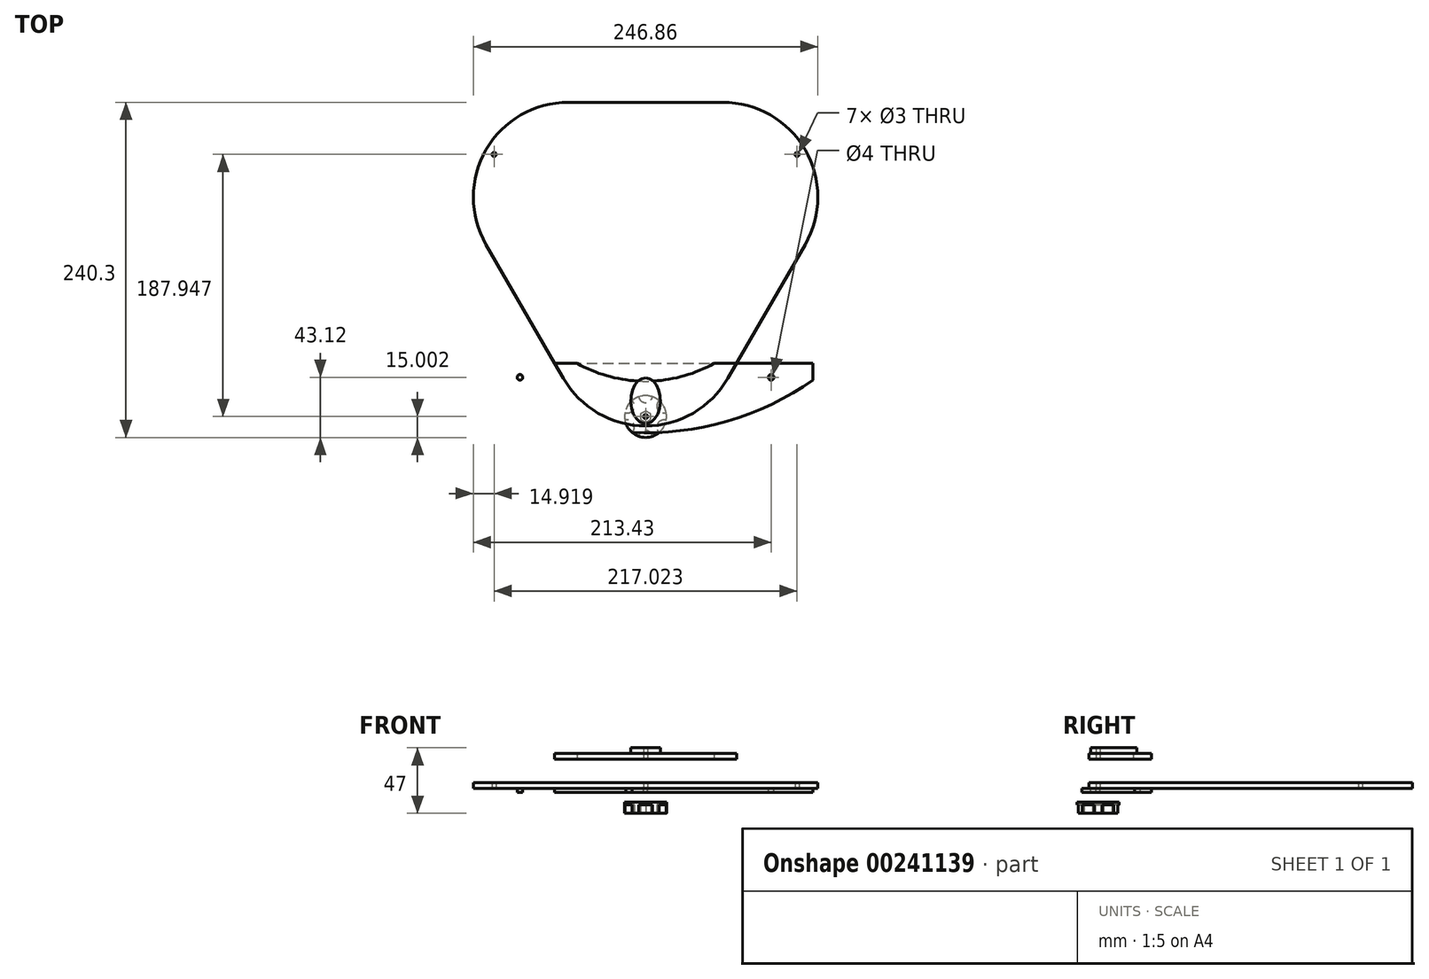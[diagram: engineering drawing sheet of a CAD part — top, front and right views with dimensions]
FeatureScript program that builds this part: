
annotation { "Feature Type Name" : "Feature", "Feature Type Description" : "" }
export const myFeature = defineFeature(function(context is Context, id is Id, definition is map)
    precondition{}
    {
        {
            var Q0;
            Q0=qCreatedBy(makeId("Top.planeOp"),FACE);
            var sketch = newSketch(context, id + "F0", { "sketchPlane" : qUnion([Q0])});
            skLineSegment(sketch, "E0.bottom", {"start": v(-120, -87.18) * mm, "end": v(120, -87.18) * mm});
            skLineSegment(sketch, "E0.top", {"start": v(-120, -107.18) * mm, "end": v(120, -107.18) * mm, "construction": true});
            skCircle(sketch, "E1", {"center": v(0, 0) * mm, "radius": 100 * mm, "construction": true});
            skCircle(sketch, "E2.1.0", {"center": v(-90, -97.18) * mm, "radius": 2 * mm});
            skCircle(sketch, "E2.1.2", {"center": v(90, -97.18) * mm, "radius": 2 * mm});
            skArc(sketch, "E3", {"start": v(-134.08, -88.82) * mm, "mid": v(-0.24, -137) * mm, "end": v(133.6, -88.82) * mm});
            skLineSegment(sketch, "E4", {"start": v(-120, -87.18) * mm, "end": v(-120, -99.5) * mm});
            skCircle(sketch, "E5", {"center": v(0, -125.3) * mm, "radius": 15 * mm});
            skPoint(sketch, "E5.centerSnap0", {"position": v(0, -107.18) * mm});
            skCircle(sketch, "E6", {"center": v(0, -125.3) * mm, "radius": 1.5 * mm});
            skLineSegment(sketch, "E7", {"start": v(120, -87.18) * mm, "end": v(120, -99.17) * mm});
            skCircle(sketch, "E8.cCircle", {"center": v(0, 0) * mm, "radius": 100 * mm});
            skLineSegment(sketch, "E8.0", {"start": v(-55.43, 100) * mm, "end": v(55.43, 100) * mm});
            skLineSegment(sketch, "E8.1", {"start": v(114.32, -2) * mm, "end": v(58.89, -98) * mm});
            skLineSegment(sketch, "E8.2", {"start": v(-58.89, -98) * mm, "end": v(-114.32, -2) * mm});
            skPoint(sketch, "E8.0.midPoint", {"position": v(0, 100) * mm});
            skCircle(sketch, "E9.1.0", {"center": v(108.51, 62.65) * mm, "radius": 1.5 * mm});
            skCircle(sketch, "E9.2.0", {"center": v(-108.51, 62.65) * mm, "radius": 1.5 * mm});
            skPoint(sketch, "E10.visualSharp", {"position": v(0, -200) * mm});
            skArc(sketch, "E10.filletArc", {"start": v(-58.89, -98) * mm, "mid": v(0, -132) * mm, "end": v(58.89, -98) * mm});
            skPoint(sketch, "E11.visualSharp", {"position": v(-173.2, 100) * mm});
            skArc(sketch, "E11.filletArc", {"start": v(-55.43, 100) * mm, "mid": v(-114.32, 66) * mm, "end": v(-114.32, -2) * mm});
            skPoint(sketch, "E12.visualSharp", {"position": v(173.2, 100) * mm});
            skArc(sketch, "E12.filletArc", {"start": v(114.32, -2) * mm, "mid": v(114.32, 66) * mm, "end": v(55.43, 100) * mm});
            skSolve(sketch);
        }
        {
            var Q0;
            Q0=makeQuery(id+"F0.imprint","IMPRINT",FACE,{"disambiguationData":[TD([[makeQuery(id+"F0.imprint","IMPRINT",EDGE,{"derivedFrom":sQuery(id+"F0.wireOp",EDGE,"E6")}),-1.0]])]});
            var Q1;
            {var subQ1=sQuery(id+"F0.wireOp",EDGE,"E8.2");var subQ3=sQuery(id+"F0.wireOp",EDGE,"E0.bottom");var subQ4=makeQuery(id+"F0.imprint","INTERSECT",VERTEX,{"derivedFrom":[subQ3,subQ1]});Q1=makeQuery(id+"F0.imprint","IMPRINT",FACE,{"disambiguationData":[TD([[makeQuery(id+"F0.imprint","IMPRINT",EDGE,{"disambiguationData":[TD([[subQ4,-1.0]])],"derivedFrom":subQ3}),-1.0]])]});}
            var Q2;
            Q2=makeQuery(id+"F0.imprint","IMPRINT",FACE,{"disambiguationData":[TD([[makeQuery(id+"F0.imprint","IMPRINT",EDGE,{"derivedFrom":sQuery(id+"F0.wireOp",EDGE,"E8.0")}),-1.0]])]});
            var Q3;
            {var subQ0=sQuery(id+"F0.wireOp",EDGE,"E8.2");var subQ1=sQuery(id+"F0.wireOp",EDGE,"E0.bottom");var subQ2=makeQuery(id+"F0.imprint","INTERSECT",VERTEX,{"derivedFrom":[subQ1,subQ0]});Q3=makeQuery(id+"F0.imprint","IMPRINT",FACE,{"disambiguationData":[TD([[makeQuery(id+"F0.imprint","IMPRINT",EDGE,{"disambiguationData":[TD([[subQ2,-1.0]])],"derivedFrom":subQ1}),1.0]])]});}
            var Q4;
            {var subQ0=sQuery(id+"F0.wireOp",EDGE,"E8.cCircle");var subQ2=sQuery(id+"F0.wireOp",EDGE,"E0.bottom");var subQ5=makeQuery(id+"F0.imprint","INTERSECT",VERTEX,{"disambiguationData":[OD(0.0)],"derivedFrom":[subQ2,subQ0]});Q4=makeQuery(id+"F0.imprint","IMPRINT",FACE,{"disambiguationData":[TD([[makeQuery(id+"F0.imprint","IMPRINT",EDGE,{"disambiguationData":[TD([[subQ5,-1.0]])],"derivedFrom":subQ2}),1.0]])]});}
            var Q5;
            {var subQ0=sQuery(id+"F0.wireOp",EDGE,"E8.cCircle");var subQ1=sQuery(id+"F0.wireOp",EDGE,"E0.bottom");var subQ2=makeQuery(id+"F0.imprint","INTERSECT",VERTEX,{"disambiguationData":[OD(0.0)],"derivedFrom":[subQ1,subQ0]});Q5=makeQuery(id+"F0.imprint","IMPRINT",FACE,{"disambiguationData":[TD([[makeQuery(id+"F0.imprint","IMPRINT",EDGE,{"disambiguationData":[TD([[subQ2,-1.0]])],"derivedFrom":subQ1}),-1.0]])]});}
            var Q6;
            {var subQ0=sQuery(id+"F0.wireOp",EDGE,"E8.1");var subQ1=sQuery(id+"F0.wireOp",EDGE,"E0.bottom");var subQ2=makeQuery(id+"F0.imprint","INTERSECT",VERTEX,{"derivedFrom":[subQ1,subQ0]});Q6=makeQuery(id+"F0.imprint","IMPRINT",FACE,{"disambiguationData":[TD([[makeQuery(id+"F0.imprint","IMPRINT",EDGE,{"disambiguationData":[TD([[subQ2,1.0]])],"derivedFrom":subQ1}),1.0]])]});}
            extrude(context, id + "F1", {"entities" : qUnion([Q0, Q1, Q2, Q3, Q4, Q5, Q6]), "depth" : 4 * mm, "offsetDistance" : 25 * mm});
        }
        {
            var Q0;
            Q0=makeQuery(id+"F0.imprint","IMPRINT",FACE,{"disambiguationData":[TD([[makeQuery(id+"F0.imprint","IMPRINT",EDGE,{"derivedFrom":sQuery(id+"F0.wireOp",EDGE,"E2.1.0")}),1.0]])]});
            var Q1;
            {var subQ1=sQuery(id+"F0.wireOp",EDGE,"E0.bottom");var subQ10=sQuery(id+"F0.wireOp",EDGE,"E8.2");var subQ11=makeQuery(id+"F0.imprint","INTERSECT",VERTEX,{"derivedFrom":[subQ1,subQ10]});Q1=makeQuery(id+"F0.imprint","IMPRINT",FACE,{"disambiguationData":[TD([[makeQuery(id+"F0.imprint","IMPRINT",EDGE,{"disambiguationData":[TD([[subQ11,-1.0]])],"derivedFrom":subQ1}),-1.0]])]});}
            var Q2;
            Q2=makeQuery(id+"F0.imprint","IMPRINT",FACE,{"disambiguationData":[TD([[makeQuery(id+"F0.imprint","IMPRINT",EDGE,{"derivedFrom":sQuery(id+"F0.wireOp",EDGE,"E6")}),-1.0]])]});
            var Q3;
            Q3=makeQuery(id+"F0.imprint","IMPRINT",FACE,{"disambiguationData":[TD([[makeQuery(id+"F0.imprint","IMPRINT",EDGE,{"derivedFrom":sQuery(id+"F0.wireOp",EDGE,"E2.1.2")}),-1.0]])]});
            var Q4;
            {var subQ0=sQuery(id+"F0.wireOp",EDGE,"E8.cCircle");var subQ1=sQuery(id+"F0.wireOp",EDGE,"E0.bottom");var subQ2=makeQuery(id+"F0.imprint","INTERSECT",VERTEX,{"disambiguationData":[OD(0.0)],"derivedFrom":[subQ1,subQ0]});Q4=makeQuery(id+"F0.imprint","IMPRINT",FACE,{"disambiguationData":[TD([[makeQuery(id+"F0.imprint","IMPRINT",EDGE,{"disambiguationData":[TD([[subQ2,-1.0]])],"derivedFrom":subQ1}),-1.0]])]});}
            var Q5;
            {var subQ0=sQuery(id+"F0.wireOp",EDGE,"E5");var subQ1=sQuery(id+"F0.wireOp",EDGE,"E3");var subQ2=makeQuery(id+"F0.imprint","INTERSECT",VERTEX,{"disambiguationData":[OD(0.0)],"derivedFrom":[subQ1,subQ0]});Q5=makeQuery(id+"F0.imprint","IMPRINT",FACE,{"disambiguationData":[TD([[makeQuery(id+"F0.imprint","IMPRINT",EDGE,{"disambiguationData":[TD([[subQ2,-1.0]])],"derivedFrom":subQ1}),1.0]])]});}
            extrude(context, id + "F2", {"entities" : qUnion([Q0, Q1, Q2, Q3, Q4, Q5]), "oppositeDirection" : true, "depth" : 3 * mm, "offsetDistance" : 25 * mm});
        }
        {
            var Q0;
            Q0=makeQuery(id+"F0.imprint","IMPRINT",FACE,{"disambiguationData":[TD([[makeQuery(id+"F0.imprint","IMPRINT",EDGE,{"derivedFrom":sQuery(id+"F0.wireOp",EDGE,"E6")}),-1.0]])]});
            var Q1;
            {var subQ0=sQuery(id+"F0.wireOp",EDGE,"E5");var subQ1=sQuery(id+"F0.wireOp",EDGE,"E3");var subQ2=makeQuery(id+"F0.imprint","INTERSECT",VERTEX,{"disambiguationData":[OD(0.0)],"derivedFrom":[subQ1,subQ0]});Q1=makeQuery(id+"F0.imprint","IMPRINT",FACE,{"disambiguationData":[TD([[makeQuery(id+"F0.imprint","IMPRINT",EDGE,{"disambiguationData":[TD([[subQ2,-1.0]])],"derivedFrom":subQ1}),1.0]])]});}
            var Q2;
            {var subQ0=sQuery(id+"F0.wireOp",EDGE,"E5");var subQ1=sQuery(id+"F0.wireOp",EDGE,"E3");var subQ2=makeQuery(id+"F0.imprint","INTERSECT",VERTEX,{"disambiguationData":[OD(0.0)],"derivedFrom":[subQ1,subQ0]});Q2=makeQuery(id+"F0.imprint","IMPRINT",FACE,{"disambiguationData":[TD([[makeQuery(id+"F0.imprint","IMPRINT",EDGE,{"disambiguationData":[TD([[subQ2,-1.0]])],"derivedFrom":subQ1}),-1.0]])]});}
            extrude(context, id + "F3", {"entities" : qUnion([Q0, Q1, Q2]), "oppositeDirection" : true, "depth" : 18 * mm, "offsetDistance" : 25 * mm, "hasSecondDirection" : true, "secondDirectionOppositeDirection" : true, "secondDirectionDepth" : 10 * mm});
        }
        {
            var Q0;
            Q0=makeQuery(id+"F3.opExtrude","CAP_FACE",FACE,{"disambiguationData":[OSD([sQuery(id+"F0.wireOp",EDGE,"E5"),sQuery(id+"F0.wireOp",EDGE,"E6")])],"isStart":false});
            var sketch = newSketch(context, id + "F4", { "sketchPlane" : qUnion([Q0])});
            skCircle(sketch, "E13", {"center": v(0, 140.3) * mm, "radius": 5 * mm});
            skCircle(sketch, "E14.1.0", {"center": v(-13, 132.8) * mm, "radius": 5 * mm});
            skCircle(sketch, "E14.2.0", {"center": v(-13, 117.8) * mm, "radius": 5 * mm});
            skPoint(sketch, "E14.center", {"position": v(0, 125.3) * mm});
            skCircle(sketch, "E15.1.3.0", {"center": v(0, 110.3) * mm, "radius": 5 * mm});
            skCircle(sketch, "E15.1.4.0", {"center": v(13, 117.8) * mm, "radius": 5 * mm});
            skCircle(sketch, "E15.1.5.0", {"center": v(13, 132.8) * mm, "radius": 5 * mm});
            skCircle(sketch, "E16.cCircle", {"center": v(0, 125.3) * mm, "radius": 3.5 * mm, "construction": true});
            skLineSegment(sketch, "E16.0", {"start": v(3.5, 127.32) * mm, "end": v(3.5, 123.28) * mm});
            skLineSegment(sketch, "E16.1", {"start": v(3.5, 123.28) * mm, "end": v(0, 121.26) * mm});
            skLineSegment(sketch, "E16.2", {"start": v(0, 121.26) * mm, "end": v(-3.5, 123.28) * mm});
            skLineSegment(sketch, "E16.3", {"start": v(-3.5, 123.28) * mm, "end": v(-3.5, 127.32) * mm});
            skLineSegment(sketch, "E16.4", {"start": v(-3.5, 127.32) * mm, "end": v(0, 129.34) * mm});
            skLineSegment(sketch, "E16.5", {"start": v(0, 129.34) * mm, "end": v(3.5, 127.32) * mm});
            skPoint(sketch, "E16.0.midPoint", {"position": v(3.5, 125.3) * mm});
            skSolve(sketch);
        }
        {
            var Q0;
            {var subQ0=sQuery(id+"F4.wireOp",EDGE,"E14.1.0");var subQ1=makeQuery(id+"F3.opExtrude","CAP_EDGE",EDGE,{"disambiguationData":[OSD([sQuery(id+"F0.wireOp",EDGE,"E5")])],"isStart":false});var subQ2=makeQuery(id+"F4.imprint","INTERSECT",VERTEX,{"disambiguationData":[OD(0.0)],"derivedFrom":[subQ1,subQ0]});Q0=makeQuery(id+"F4.imprint","IMPRINT",FACE,{"disambiguationData":[TD([[makeQuery(id+"F4.imprint","IMPRINT",EDGE,{"disambiguationData":[TD([[subQ2,-1.0]])],"derivedFrom":subQ0}),1.0]])]});}
            var Q1;
            {var subQ0=sQuery(id+"F4.wireOp",EDGE,"E13");var subQ1=makeQuery(id+"F3.opExtrude","CAP_EDGE",EDGE,{"disambiguationData":[OSD([sQuery(id+"F0.wireOp",EDGE,"E5")])],"isStart":false});var subQ2=makeQuery(id+"F4.imprint","INTERSECT",VERTEX,{"disambiguationData":[OD(0.0)],"derivedFrom":[subQ1,subQ0]});Q1=makeQuery(id+"F4.imprint","IMPRINT",FACE,{"disambiguationData":[TD([[makeQuery(id+"F4.imprint","IMPRINT",EDGE,{"disambiguationData":[TD([[subQ2,-1.0]])],"derivedFrom":subQ0}),1.0]])]});}
            var Q2;
            {var subQ0=sQuery(id+"F4.wireOp",EDGE,"E15.1.5.0");var subQ1=makeQuery(id+"F3.opExtrude","CAP_EDGE",EDGE,{"disambiguationData":[OSD([sQuery(id+"F0.wireOp",EDGE,"E5")])],"isStart":false});var subQ2=makeQuery(id+"F4.imprint","INTERSECT",VERTEX,{"disambiguationData":[OD(0.0)],"derivedFrom":[subQ1,subQ0]});Q2=makeQuery(id+"F4.imprint","IMPRINT",FACE,{"disambiguationData":[TD([[makeQuery(id+"F4.imprint","IMPRINT",EDGE,{"disambiguationData":[TD([[subQ2,-1.0]])],"derivedFrom":subQ0}),1.0]])]});}
            var Q3;
            {var subQ0=sQuery(id+"F4.wireOp",EDGE,"E15.1.4.0");var subQ1=makeQuery(id+"F3.opExtrude","CAP_EDGE",EDGE,{"disambiguationData":[OSD([sQuery(id+"F0.wireOp",EDGE,"E5")])],"isStart":false});var subQ2=makeQuery(id+"F4.imprint","INTERSECT",VERTEX,{"disambiguationData":[OD(0.0)],"derivedFrom":[subQ1,subQ0]});Q3=makeQuery(id+"F4.imprint","IMPRINT",FACE,{"disambiguationData":[TD([[makeQuery(id+"F4.imprint","IMPRINT",EDGE,{"disambiguationData":[TD([[subQ2,1.0]])],"derivedFrom":subQ0}),1.0]])]});}
            var Q4;
            {var subQ0=sQuery(id+"F4.wireOp",EDGE,"E15.1.3.0");var subQ1=makeQuery(id+"F3.opExtrude","CAP_EDGE",EDGE,{"disambiguationData":[OSD([sQuery(id+"F0.wireOp",EDGE,"E5")])],"isStart":false});var subQ2=makeQuery(id+"F4.imprint","INTERSECT",VERTEX,{"disambiguationData":[OD(0.0)],"derivedFrom":[subQ1,subQ0]});Q4=makeQuery(id+"F4.imprint","IMPRINT",FACE,{"disambiguationData":[TD([[makeQuery(id+"F4.imprint","IMPRINT",EDGE,{"disambiguationData":[TD([[subQ2,1.0]])],"derivedFrom":subQ0}),1.0]])]});}
            var Q5;
            {var subQ0=sQuery(id+"F4.wireOp",EDGE,"E14.2.0");var subQ1=makeQuery(id+"F3.opExtrude","CAP_EDGE",EDGE,{"disambiguationData":[OSD([sQuery(id+"F0.wireOp",EDGE,"E5")])],"isStart":false});var subQ2=makeQuery(id+"F4.imprint","INTERSECT",VERTEX,{"disambiguationData":[OD(0.0)],"derivedFrom":[subQ1,subQ0]});Q5=makeQuery(id+"F4.imprint","IMPRINT",FACE,{"disambiguationData":[TD([[makeQuery(id+"F4.imprint","IMPRINT",EDGE,{"disambiguationData":[TD([[subQ2,1.0]])],"derivedFrom":subQ0}),1.0]])]});}
            var Q6;
            Q6=makeQuery(id+"F4.imprint","IMPRINT",FACE,{"disambiguationData":[TD([[makeQuery(id+"F4.imprint","IMPRINT",EDGE,{"derivedFrom":sQuery(id+"F4.wireOp",EDGE,"E16.0")}),-1.0]])]});
            extrude(context, id + "F5", {"entities" : qUnion([Q0, Q1, Q2, Q3, Q4, Q5, Q6]), "operationType" : NewBodyOperationType.REMOVE, "oppositeDirection" : true, "depth" : 6 * mm, "offsetDistance" : 25 * mm});
        }
        {
            var Q0;
            Q0=makeQuery(id+"F0.imprint","IMPRINT",FACE,{"disambiguationData":[TD([[makeQuery(id+"F0.imprint","IMPRINT",EDGE,{"derivedFrom":sQuery(id+"F0.wireOp",EDGE,"E6")}),-1.0]])]});
            var Q1;
            {var subQ1=sQuery(id+"F0.wireOp",EDGE,"E0.bottom");var subQ10=sQuery(id+"F0.wireOp",EDGE,"E8.2");var subQ11=makeQuery(id+"F0.imprint","INTERSECT",VERTEX,{"derivedFrom":[subQ1,subQ10]});Q1=makeQuery(id+"F0.imprint","IMPRINT",FACE,{"disambiguationData":[TD([[makeQuery(id+"F0.imprint","IMPRINT",EDGE,{"disambiguationData":[TD([[subQ11,-1.0]])],"derivedFrom":subQ1}),-1.0]])]});}
            extrude(context, id + "F6", {"entities" : qUnion([Q0, Q1]), "depth" : 25 * mm, "offsetDistance" : 25 * mm, "hasSecondDirection" : true, "secondDirectionOppositeDirection" : false, "secondDirectionDepth" : 21 * mm});
        }
        {
            var Q0;
            Q0=makeQuery(id+"F6.opExtrude","CAP_FACE",FACE,{"disambiguationData":[OSD([sQuery(id+"F0.wireOp",EDGE,"E0.bottom"),sQuery(id+"F0.wireOp",EDGE,"E6"),sQuery(id+"F0.wireOp",EDGE,"E8.cCircle"),sQuery(id+"F0.wireOp",EDGE,"E8.1"),sQuery(id+"F0.wireOp",EDGE,"E8.2"),sQuery(id+"F0.wireOp",EDGE,"E10.filletArc")])],"isStart":false});
            var sketch = newSketch(context, id + "F7", { "sketchPlane" : qUnion([Q0])});
            skEllipse(sketch, "E17", {"center": v(0, -114) * mm, "majorRadius": 16.5 * mm, "minorRadius": 10.56 * mm, "majorAxis": v(0, 1)});
            skSolve(sketch);
        }
        {
            var Q0;
            Q0=makeQuery(id+"F7.imprint","IMPRINT",FACE,{"disambiguationData":[TD([[makeQuery(id+"F7.imprint","IMPRINT",EDGE,{"derivedFrom":makeQuery(id+"F6.opExtrude","CAP_EDGE",EDGE,{"disambiguationData":[OSD([sQuery(id+"F0.wireOp",EDGE,"E6")])],"isStart":false})}),-1.0]])]});
            var Q1;
            {var subQ0=sQuery(id+"F7.wireOp",EDGE,"E17");var subQ1=makeQuery(id+"F6.opExtrude","CAP_EDGE",EDGE,{"disambiguationData":[OSD([sQuery(id+"F0.wireOp",EDGE,"E8.cCircle")])],"isStart":false});var subQ2=makeQuery(id+"F7.imprint","INTERSECT",VERTEX,{"disambiguationData":[OD(0.0)],"derivedFrom":[subQ1,subQ0]});Q1=makeQuery(id+"F7.imprint","IMPRINT",FACE,{"disambiguationData":[TD([[makeQuery(id+"F7.imprint","IMPRINT",EDGE,{"disambiguationData":[TD([[subQ2,1.0]])],"derivedFrom":subQ0}),1.0]])]});}
            extrude(context, id + "F8", {"entities" : qUnion([Q0, Q1]), "depth" : 4 * mm, "offsetDistance" : 25 * mm});
        }
    });
